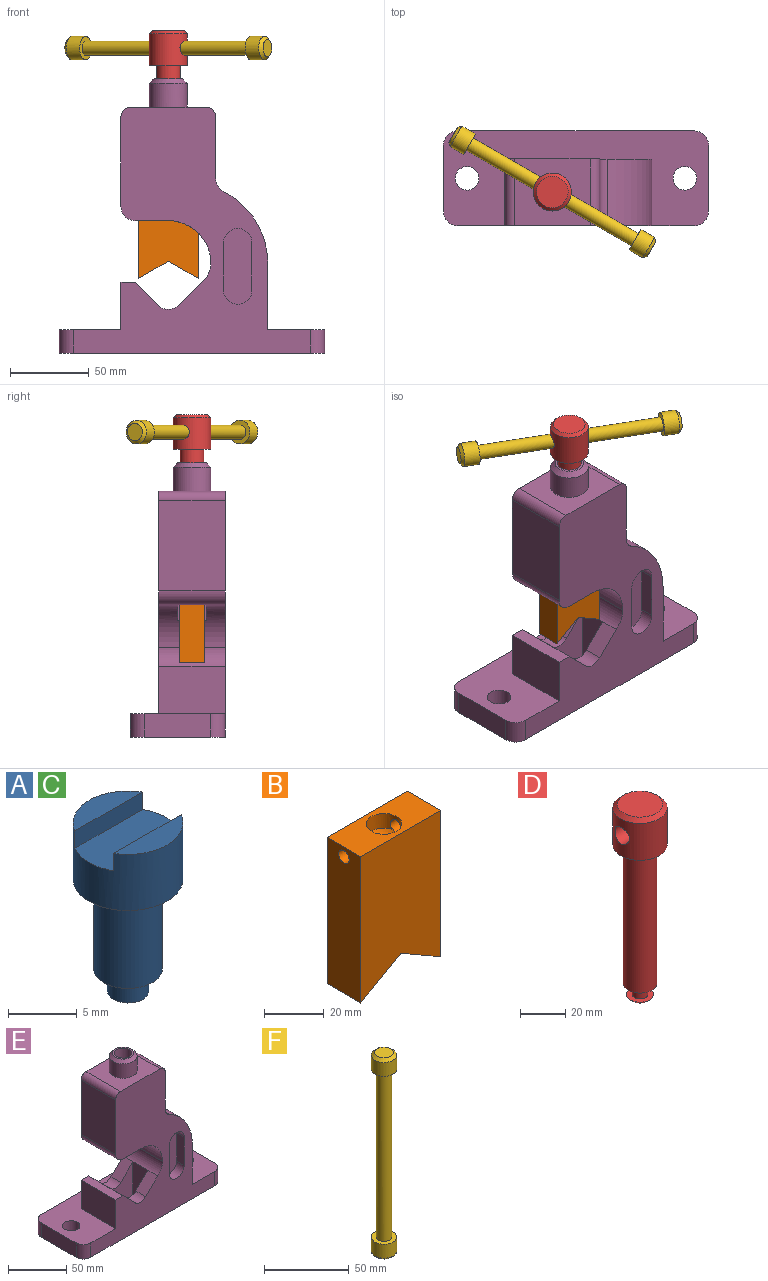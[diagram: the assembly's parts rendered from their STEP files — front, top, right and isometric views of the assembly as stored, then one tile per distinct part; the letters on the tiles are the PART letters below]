
ASSEMBLY  parts=6 mates=5
PART A: 11 faces, bbox 8x8x15 mm
  f0: plane 6.93x2mm, normal (0,0,1), area 9.8mm2, adj f1,f9
  f1: cylinder r=4mm len=8mm, axis (0,0,-1), area 112.7mm2, adj f0,f2,f7,f8,f9,f10
  f2: plane 6.93x2mm, normal (0,0,1), area 9.8mm2, adj f1,f8
  f3: plane 3x3mm, normal (0,0,-1), area 7.1mm2, adj f4
  f4: cylinder r=1.5mm len=3mm, axis (0,0,-1), area 18.8mm2, adj f3,f5
  f5: plane 5x5mm, normal (0,0,-1), area 12.6mm2, adj f4,f6
  f6: cylinder r=2.5mm len=8mm, axis (0,0,-1), area 125.7mm2, adj f5,f7
  f7: plane 8x8mm, normal (0,0,-1), area 30.6mm2, adj f1,f6
  f8: plane 6.93x1.55mm, normal (0,-1,0), area 10.8mm2, adj f1,f2,f10
  f9: plane 6.93x1.55mm, normal (0,1,0), area 10.8mm2, adj f0,f1,f10
  f10: plane 8x4mm, normal (0,0,1), area 30.6mm2, adj f1,f8,f9
PART B: 11 faces, bbox 38x16x60 mm
  f0: plane 38x16mm, normal (0,0,1), area 494.9mm2, adj f1,f4,f5,f6,f7
  f1: plane 60x16mm, normal (-1,0,0), area 940.4mm2, adj f0,f2,f5,f6,f9
  f2: plane 19x16mm, normal (0.5,0,-0.87), area 351mm2, adj f1,f3,f5,f6
  f3: plane 19x16mm, normal (-0.5,0,-0.87), area 351mm2, adj f2,f4,f5,f6
  f4: plane 60x16mm, normal (1,0,0), area 940.4mm2, adj f0,f3,f5,f6,f10
  f5: plane 60x38mm, normal (0,-1,0), area 2071.6mm2, adj f0,f1,f2,f3,f4
  f6: plane 60x38mm, normal (0,1,0), area 2071.6mm2, adj f0,f1,f2,f3,f4
  f7: cylinder r=6mm len=12mm, axis (0,0,1), area 188.1mm2, adj f0,f8,f9,f10
  f8: sphere r=7.5mm, area 138.7mm2, adj f7,f9,f10
  f9: cylinder r=2.5mm len=13.55mm, axis (1,0,0), area 209.3mm2, adj f1,f7,f8
  f10: cylinder r=2.5mm len=13.55mm, axis (1,0,0), area 209.3mm2, adj f4,f7,f8
PART C: same geometry as A
PART D: 12 faces, bbox 24x24x106 mm
  f0: plane 20x20mm, normal (0,0,1), area 314.2mm2, adj f11
  f1: sphere r=7.5mm, area 141.4mm2, adj f2
  f2: plane 12x12mm, normal (0,0,1), area 74.6mm2, adj f1,f3
  f3: cylinder r=3.5mm len=7mm, axis (0,0,1), area 110mm2, adj f2,f4
  f4: plane 8x8mm, normal (0,0,-1), area 11.8mm2, adj f3,f5
  f5: cylinder r=4mm len=8mm, axis (0,0,1), area 25.1mm2, adj f4,f6
  f6: plane 15x15mm, normal (0,0,-1), area 126.4mm2, adj f5,f7
  f7: cylinder r=7.5mm len=75mm, axis (0,0,1), area 3534.3mm2, adj f6,f8
  f8: plane 24x24mm, normal (0,0,-1), area 275.7mm2, adj f7,f9
  f9: cylinder r=12mm len=24mm, axis (0,0,1), area 1378.5mm2, adj f8,f10,f11
  f10: cylinder r=4.5mm len=24mm, axis (1,0,0), area 654mm2, adj f9
  f11: cone r=10mm half-angle=45deg, axis (0,0,-1), area 195.5mm2, adj f0,f9
PART E: 59 faces, bbox 168x60x174 mm
  f0: plane 141x93mm, normal (0,1,0), area 7700.2mm2, adj f3,f4,f5,f6,f7,f17,f18,f19
  f1: plane 156x150mm, normal (0,-1,0), area 9950.2mm2, adj f2,f4,f11,f12,f17,f18,f19,f20
  f2: plane 168x60mm, normal (0,0,-1), area 8901mm2, adj f1,f8,f9,f10,f11,f12,f13,f14
  f3: plane 21x12mm, normal (0,0,-1), area 252mm2, adj f0,f4,f27,f41
  f4: cylinder r=27mm len=42mm, axis (0,-1,0), area 1348.2mm2, adj f0,f1,f3,f28,f29,f40,f41,f42
  f5: plane 14.64x14.64mm, normal (-0.71,0,0.71), area 248.4mm2, adj f0,f6,f29,f38
  f6: cylinder r=9mm len=12.73mm, axis (0,-1,0), area 169.6mm2, adj f0,f5,f7,f38
  f7: plane 14.64x14.64mm, normal (0.71,0,0.71), area 248.4mm2, adj f0,f6,f33,f38
  f8: plane 150x15mm, normal (0,1,0), area 2250mm2, adj f2,f9,f16,f17
  f9: cylinder r=9mm len=15mm, axis (0,0,-1), area 212.1mm2, adj f2,f8,f10,f17
  f10: plane 42x15mm, normal (-1,0,0), area 630mm2, adj f2,f9,f11,f17
  f11: cylinder r=9mm len=15mm, axis (0,0,-1), area 212.1mm2, adj f1,f2,f10,f17
  f12: cylinder r=9mm len=15mm, axis (0,0,-1), area 212.1mm2, adj f1,f2,f13,f17
  f13: plane 42x15mm, normal (1,0,0), area 630mm2, adj f2,f12,f16,f17
  f14: cylinder r=7.5mm len=15mm, axis (0,0,-1), area 706.9mm2, adj f2,f17
  f15: cylinder r=7.5mm len=15mm, axis (0,0,-1), area 706.9mm2, adj f2,f17
  f16: cylinder r=9mm len=15mm, axis (0,0,-1), area 212.1mm2, adj f2,f8,f13,f17
  f17: plane 168x60mm, normal (0,0,1), area 5751mm2, adj f0,f1,f8,f9,f10,f11,f12,f13
  f18: plane 42x30mm, normal (-1,0,0), area 1260mm2, adj f0,f1,f17,f33
  f19: plane 42x42mm, normal (1,0,0), area 1764mm2, adj f0,f1,f17,f20
  f20: cylinder r=51mm len=45.54mm, axis (0,-1,0), area 2364.8mm2, adj f0,f1,f19,f21
  f21: cylinder r=9mm len=42mm, axis (0,-1,0), area 417.3mm2, adj f0,f1,f20,f22
  f22: plane 42x39.42mm, normal (1,0,0), area 1655.6mm2, adj f0,f1,f21,f23
  f23: cylinder r=6mm len=42mm, axis (0,-1,0), area 395.8mm2, adj f0,f1,f22,f24
  f24: plane 48x42mm, normal (0,0,1), area 1563.6mm2, adj f0,f1,f23,f25,f34
  f25: cylinder r=6mm len=42mm, axis (0,-1,0), area 395.8mm2, adj f0,f1,f24,f26
  f26: plane 57x42mm, normal (-1,0,0), area 2394mm2, adj f0,f1,f25,f27
  f27: cylinder r=9mm len=42mm, axis (0,-1,0), area 593.8mm2, adj f0,f1,f3,f26,f28,f43
  f28: plane 21x12mm, normal (0,0,-1), area 252mm2, adj f1,f4,f27,f42
  f29: cylinder r=15mm len=42mm, axis (0,-1,0), area 584.2mm2, adj f0,f1,f4,f5,f30,f39
  f30: plane 14.64x14.64mm, normal (-0.71,0,0.71), area 248.4mm2, adj f1,f29,f31,f37
  f31: cylinder r=9mm len=12.73mm, axis (0,-1,0), area 169.6mm2, adj f1,f30,f32,f37
  f32: plane 14.64x14.64mm, normal (0.71,0,0.71), area 248.4mm2, adj f1,f31,f33,f37
  f33: plane 42x9mm, normal (0,0,1), area 378mm2, adj f0,f1,f7,f18,f32,f36
  f34: cylinder r=12mm len=24mm, axis (0,0,-1), area 1131mm2, adj f24,f58
  f35: plane 18x18mm, normal (0,0,1), area 77.8mm2, adj f47,f58
  f36: plane 45x18mm, normal (1,0,0), area 810mm2, adj f2,f33,f37,f38
  f37: plane 45x42mm, normal (0,1,0), area 1466.4mm2, adj f2,f30,f31,f32,f36,f39
  f38: plane 45x42mm, normal (0,-1,0), area 1466.4mm2, adj f2,f5,f6,f7,f36,f39
  f39: plane 45x18mm, normal (-1,0,0), area 810mm2, adj f2,f29,f37,f38
  f40: plane 61.03x18mm, normal (-1,0,0), area 1098.5mm2, adj f4,f41,f42,f44
  f41: plane 70.03x42mm, normal (0,-1,0), area 2549.2mm2, adj f3,f4,f40,f43,f44,f45,f46
  f42: plane 70.03x42mm, normal (0,1,0), area 2549.2mm2, adj f4,f28,f40,f43,f44,f45,f46
  f43: plane 51x18mm, normal (1,0,0), area 918mm2, adj f27,f41,f42,f46
  f44: cylinder r=9mm len=18mm, axis (0,-1,0), area 254.5mm2, adj f40,f41,f42,f45
  f45: plane 24x18mm, normal (0,0,-1), area 255.3mm2, adj f41,f42,f44,f46,f47
  f46: cylinder r=9mm len=18mm, axis (0,-1,0), area 254.5mm2, adj f41,f42,f43,f45
  f47: cylinder r=7.5mm len=30mm, axis (0,0,1), area 1413.7mm2, adj f35,f45
  f48: plane 30x9mm, normal (1,0,0), area 270mm2, adj f1,f49,f51,f52
  f49: cylinder r=9mm len=18mm, axis (0,-1,0), area 254.5mm2, adj f1,f48,f50,f52
  f50: plane 30x9mm, normal (-1,0,0), area 270mm2, adj f1,f49,f51,f52
  f51: cylinder r=9mm len=18mm, axis (0,-1,0), area 254.5mm2, adj f1,f48,f50,f52
  f52: plane 48x18mm, normal (0,-1,0), area 794.5mm2, adj f48,f49,f50,f51
  f53: plane 30x9mm, normal (1,0,0), area 270mm2, adj f0,f54,f56,f57
  f54: cylinder r=9mm len=18mm, axis (0,1,0), area 254.5mm2, adj f0,f53,f55,f57
  f55: plane 30x9mm, normal (-1,0,0), area 270mm2, adj f0,f54,f56,f57
  f56: cylinder r=9mm len=18mm, axis (0,1,0), area 254.5mm2, adj f0,f53,f55,f57
  f57: plane 48x18mm, normal (0,1,0), area 794.5mm2, adj f53,f54,f55,f56
  f58: cone r=9mm half-angle=45deg, axis (0,0,-1), area 279.9mm2, adj f34,f35
PART F: 9 faces, bbox 15x15x145 mm
  f0: cylinder r=4.5mm len=121mm, axis (0,0,1), area 3421.2mm2, adj f2,f6
  f1: cylinder r=7.5mm len=15mm, axis (0,0,1), area 471.2mm2, adj f2,f4
  f2: plane 15x15mm, normal (0,0,-1), area 113.1mm2, adj f0,f1
  f3: plane 11x11mm, normal (0,0,1), area 95mm2, adj f4
  f4: cone r=5.5mm half-angle=45deg, axis (0,0,-1), area 115.5mm2, adj f1,f3
  f5: cylinder r=7.5mm len=15mm, axis (0,0,-1), area 471.2mm2, adj f6,f8
  f6: plane 15x15mm, normal (0,0,1), area 113.1mm2, adj f0,f5
  f7: plane 11x11mm, normal (0,0,-1), area 95mm2, adj f8
  f8: cone r=5.5mm half-angle=45deg, axis (0,0,1), area 115.5mm2, adj f5,f7
PLACE A rot(axis=(0,-1,0),90deg) t=(-22.45,0,-70.67)mm
PLACE B t=(0,0,-96.67)mm
PLACE C rot(axis=(0.71,0,0.71),180deg) t=(22.45,0,-70.67)mm
PLACE D rot(axis=(0,0,-1),30deg) t=(0,0,-18.17)mm
PLACE E t=(0,9,-166.5)mm fixed
PLACE F rot(axis=(0.25,0.94,-0.25),93.8deg) t=(0,0,19.33)mm
MATE revolute B.f7 <-> D.f3  axis (0,0,1) through (0,0,-66.67)mm
MATE cylindrical D.f3 <-> E.f34  axis (0,0,1) through (0,0,-29.17)mm
MATE fastened A.f1 <-> B.f9  axis (1,0,0) through (-19,0,-70.67)mm
MATE fastened F.f0 <-> D.f10  axis (0.87,-0.5,0) through (0,0,19.33)mm
MATE fastened C.f1 <-> B.f9  axis (-1,0,0) through (19,0,-70.67)mm
